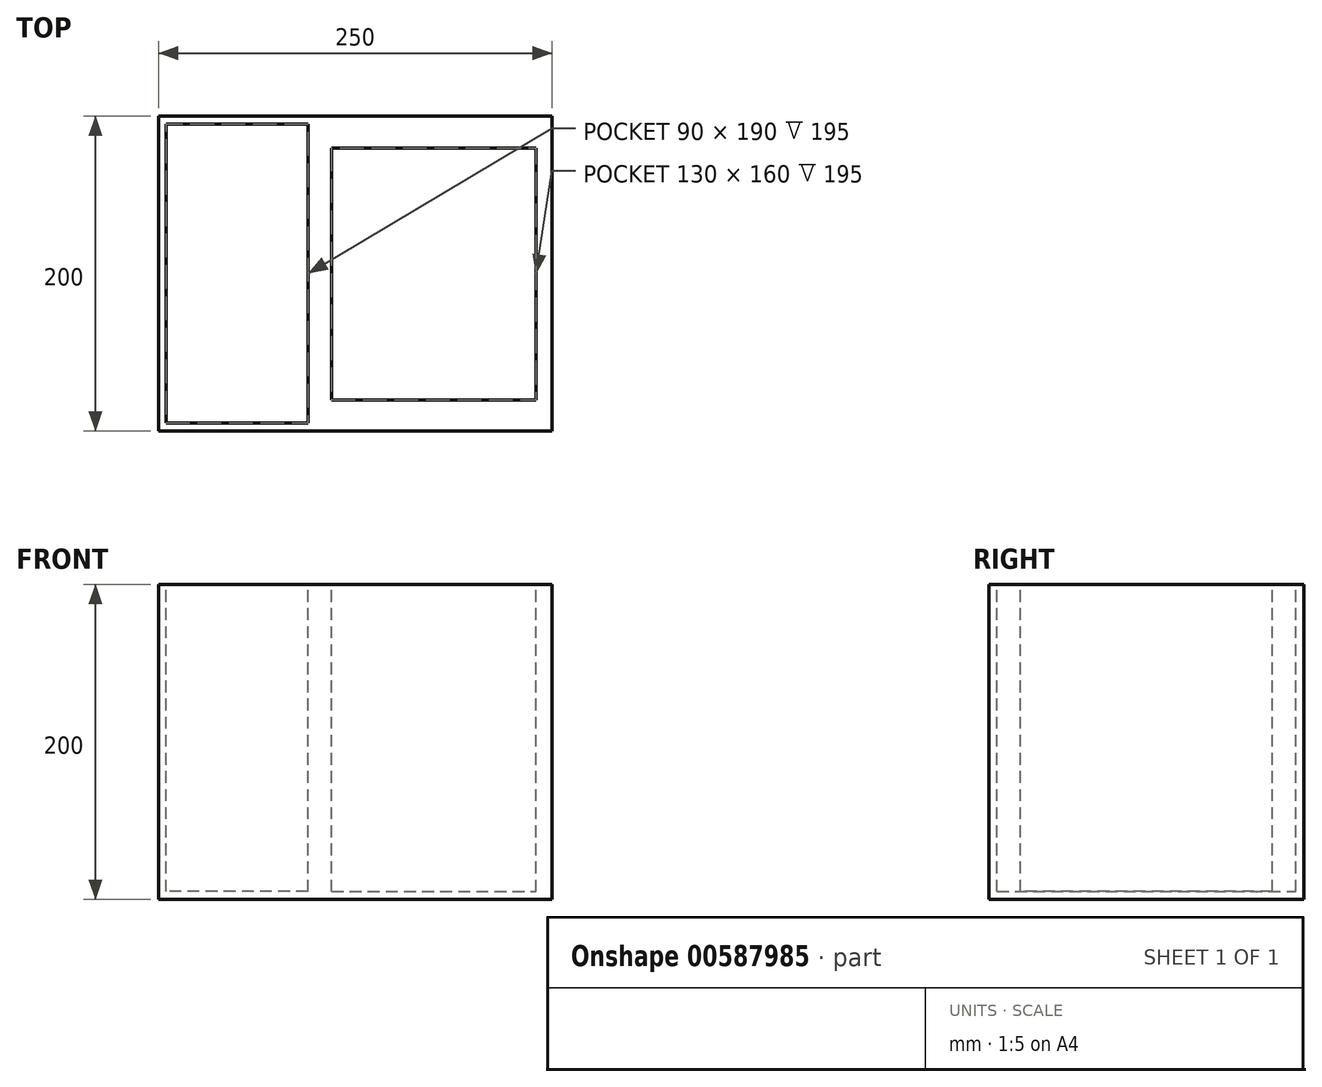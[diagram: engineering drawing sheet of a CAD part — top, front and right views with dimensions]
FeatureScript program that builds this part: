
annotation { "Feature Type Name" : "Feature", "Feature Type Description" : "" }
export const myFeature = defineFeature(function(context is Context, id is Id, definition is map)
    precondition{}
    {
        {
            var Q0;
            Q0=qCreatedBy(makeId("Top.planeOp"),FACE);
            var sketch = newSketch(context, id + "F0", { "sketchPlane" : qUnion([Q0])});
            skLineSegment(sketch, "E0.bottom", {"start": v(-50, -100) * mm, "end": v(50, -100) * mm});
            skLineSegment(sketch, "E0.top", {"start": v(-50, 100) * mm, "end": v(50, 100) * mm});
            skLineSegment(sketch, "E0.left", {"start": v(-50, -100) * mm, "end": v(-50, 100) * mm});
            skLineSegment(sketch, "E0.right", {"start": v(50, -100) * mm, "end": v(50, 100) * mm});
            skPoint(sketch, "E0.middle", {"position": v(0, 0) * mm});
            skLineSegment(sketch, "E1.bottom", {"start": v(50, 100) * mm, "end": v(200, 100) * mm});
            skLineSegment(sketch, "E1.top", {"start": v(50, -100) * mm, "end": v(200, -100) * mm});
            skLineSegment(sketch, "E1.left", {"start": v(50, 100) * mm, "end": v(50, -100) * mm});
            skLineSegment(sketch, "E1.right", {"start": v(200, 100) * mm, "end": v(200, -100) * mm});
            skSolve(sketch);
        }
        {
            var Q0;
            Q0=makeQuery(id+"F0.imprint","IMPRINT",FACE,{"disambiguationData":[TD([[makeQuery(id+"F0.imprint","IMPRINT",EDGE,{"derivedFrom":sQuery(id+"F0.wireOp",EDGE,"E0.bottom")}),1.0]])]});
            extrude(context, id + "F1", {"entities" : qUnion([Q0]), "depth" : 200 * mm, "offsetDistance" : 25 * mm});
        }
        {
            var Q0;
            Q0=makeQuery(id+"F0.imprint","IMPRINT",FACE,{"disambiguationData":[TD([[makeQuery(id+"F0.imprint","IMPRINT",EDGE,{"derivedFrom":sQuery(id+"F0.wireOp",EDGE,"E1.bottom")}),-1.0]])]});
            extrude(context, id + "F2", {"entities" : qUnion([Q0]), "operationType" : NewBodyOperationType.ADD, "depth" : 200 * mm, "offsetDistance" : 25 * mm});
        }
        {
            var Q0;
            {var subQ0=sQuery(id+"F0.wireOp",EDGE,"E1.left");Q0=makeQuery(id+"F2.boolean.opBoolean","MERGE",FACE,{"derivedFrom":[makeQuery(id+"F1.opExtrude","CAP_FACE",FACE,{"disambiguationData":[OSD([sQuery(id+"F0.wireOp",EDGE,"E0.bottom"),sQuery(id+"F0.wireOp",EDGE,"E0.top"),sQuery(id+"F0.wireOp",EDGE,"E0.left"),subQ0])],"isStart":false}),makeQuery(id+"F2.opExtrude","CAP_FACE",FACE,{"disambiguationData":[OSD([sQuery(id+"F0.wireOp",EDGE,"E1.bottom"),sQuery(id+"F0.wireOp",EDGE,"E1.top"),subQ0,sQuery(id+"F0.wireOp",EDGE,"E1.right")])],"isStart":false})]});}
            var sketch = newSketch(context, id + "F3", { "sketchPlane" : qUnion([Q0])});
            skLineSegment(sketch, "E2.bottom", {"start": v(45, -95) * mm, "end": v(-45, -95) * mm});
            skLineSegment(sketch, "E2.top", {"start": v(45, 95) * mm, "end": v(-45, 95) * mm});
            skLineSegment(sketch, "E2.left", {"start": v(45, -95) * mm, "end": v(45, 95) * mm});
            skLineSegment(sketch, "E2.right", {"start": v(-45, -95) * mm, "end": v(-45, 95) * mm});
            skPoint(sketch, "E2.middle", {"position": v(0, 0) * mm});
            skSolve(sketch);
        }
        {
            var Q0;
            Q0=makeQuery(id+"F3.imprint","IMPRINT",FACE,{"disambiguationData":[TD([[makeQuery(id+"F3.imprint","IMPRINT",EDGE,{"derivedFrom":sQuery(id+"F3.wireOp",EDGE,"E2.bottom")}),-1.0]])]});
            extrude(context, id + "F4", {"entities" : qUnion([Q0]), "operationType" : NewBodyOperationType.REMOVE, "oppositeDirection" : true, "depth" : 195 * mm, "offsetDistance" : 25 * mm});
        }
        {
            var Q0;
            {var subQ0=sQuery(id+"F0.wireOp",EDGE,"E1.left");Q0=makeQuery(id+"F2.boolean.opBoolean","MERGE",FACE,{"derivedFrom":[makeQuery(id+"F1.opExtrude","CAP_FACE",FACE,{"disambiguationData":[OSD([sQuery(id+"F0.wireOp",EDGE,"E0.bottom"),sQuery(id+"F0.wireOp",EDGE,"E0.top"),sQuery(id+"F0.wireOp",EDGE,"E0.left"),subQ0])],"isStart":false}),makeQuery(id+"F2.opExtrude","CAP_FACE",FACE,{"disambiguationData":[OSD([sQuery(id+"F0.wireOp",EDGE,"E1.bottom"),sQuery(id+"F0.wireOp",EDGE,"E1.top"),subQ0,sQuery(id+"F0.wireOp",EDGE,"E1.right")])],"isStart":false})]});}
            var sketch = newSketch(context, id + "F5", { "sketchPlane" : qUnion([Q0])});
            skPoint(sketch, "E3.firstSnap0", {"position": v(75, 100) * mm});
            skLineSegment(sketch, "E3.bottom", {"start": v(75, 64.77) * mm, "end": v(175, 64.77) * mm});
            skLineSegment(sketch, "E3.top", {"start": v(75, -65.23) * mm, "end": v(175, -65.23) * mm});
            skLineSegment(sketch, "E3.left", {"start": v(75, 64.77) * mm, "end": v(75, -65.23) * mm});
            skLineSegment(sketch, "E3.right", {"start": v(175, 64.77) * mm, "end": v(175, -65.23) * mm});
            skSolve(sketch);
        }
        {
            var Q0;
            Q0=makeQuery(id+"F5.imprint","IMPRINT",FACE,{"disambiguationData":[TD([[makeQuery(id+"F5.imprint","IMPRINT",EDGE,{"derivedFrom":sQuery(id+"F5.wireOp",EDGE,"E3.bottom")}),-1.0]])]});
            var sketch = newSketch(context, id + "F6", { "sketchPlane" : qUnion([Q0])});
            skLineSegment(sketch, "E4.0", {"start": v(60, 79.77) * mm, "end": v(190, 79.77) * mm});
            skLineSegment(sketch, "E4.1", {"start": v(60, 79.77) * mm, "end": v(60, -80.23) * mm});
            skLineSegment(sketch, "E4.2", {"start": v(60, -80.23) * mm, "end": v(190, -80.23) * mm});
            skLineSegment(sketch, "E4.3", {"start": v(190, 79.77) * mm, "end": v(190, -80.23) * mm});
            skSolve(sketch);
        }
        {
            var Q0;
            Q0=makeQuery(id+"F5.imprint","IMPRINT",FACE,{"disambiguationData":[TD([[makeQuery(id+"F5.imprint","IMPRINT",EDGE,{"derivedFrom":sQuery(id+"F5.wireOp",EDGE,"E3.bottom")}),-1.0]])]});
            extrude(context, id + "F7", {"entities" : qUnion([Q0]), "operationType" : NewBodyOperationType.REMOVE, "oppositeDirection" : true, "depth" : 195 * mm, "offsetDistance" : 25 * mm});
        }
        {
            var Q0;
            Q0 = qSketchRegion(id + "F6", true);
            var Q1;
            Q1=makeQuery(id+"F6.imprint","IMPRINT",FACE,{"disambiguationData":[TD([[makeQuery(id+"F6.imprint","IMPRINT",EDGE,{"derivedFrom":sQuery(id+"F6.wireOp",EDGE,"E4.0")}),-1.0]])]});
            extrude(context, id + "F8", {"entities" : qUnion([Q0, Q1]), "operationType" : NewBodyOperationType.REMOVE, "oppositeDirection" : true, "depth" : 195 * mm, "offsetDistance" : 25 * mm});
        }
    });
